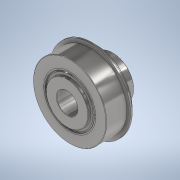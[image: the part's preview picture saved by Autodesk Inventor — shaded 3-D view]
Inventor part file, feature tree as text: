
AUTODESK INVENTOR PART (.ipt)
format: ipt  version: 2020 (Build 240168000, 168)  size: 358,400 bytes
history: native  units: in
note: dims shown in document units (in); Inventor stores cm internally (conversion verified against a paired STEP export)
features: revolve x3, fillet x2, chamfer x1, pattern_circular x1
ambient origin geometry x8: Origin, YZ Plane, XZ Plane, XY Plane, X Axis, Y Axis, Z Axis, Center Point
bodies: Solid1 (feature_tree), Solid2 (feature_tree), Solid3 (feature_tree), Solid4 (feature_tree), Solid5 (feature_tree), Solid6 (feature_tree), Solid7 (feature_tree)
feature tree (7):
  fillet  "Fillet2"  [1 undecoded]
  revolve  "Revolve3"  [1 undecoded]
  revolve  "Revolve4[1]"  [1 undecoded]
  revolve  "Revolve4[2]"  [1 undecoded]
  chamfer  "Chamfer1"  [1 undecoded]
  fillet  "Fillet1"  [1 undecoded]
  pattern_circular  "CirPattern2"
note: 6 required parameter values undecoded (feature->parameter linkage not recoverable at this tier; creation-order binding heuristic only, values carry confidence <= 0.55)
